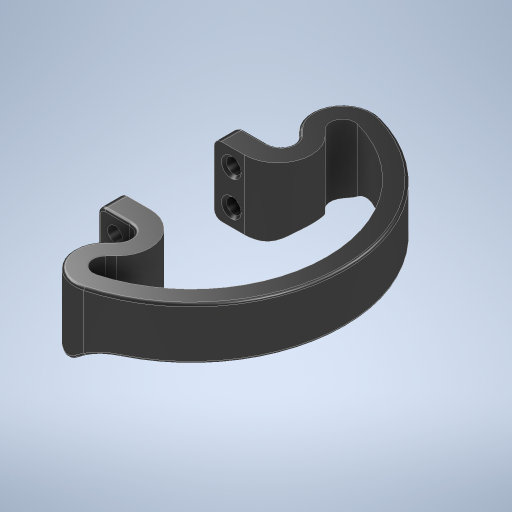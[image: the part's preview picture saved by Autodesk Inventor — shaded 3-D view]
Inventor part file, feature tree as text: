
AUTODESK INVENTOR PART (.ipt)
format: ipt  version: 2024.2 (Build 282272000, 272)  size: 499,200 bytes
history: native  units: mm
features: extrude x3, fillet x3, sketch x3, mirror x1, chamfer x1
ambient origin geometry x8: Origin, YZ Plane, XZ Plane, XY Plane, X Axis, Y Axis, Z Axis, Center Point
bodies: Solid1 (feature_tree)
feature tree (11):
  extrude  "Extrusion1"  Depth=10.0mm
  extrude  "Extrusion2"  Depth=10.0mm
  fillet  "Fillet1"  Radius=1.0mm
  extrude  "Extrusion3"  Depth=3.0mm
  mirror  "Mirror1"
  fillet  "Fillet2"  Radius=1.0mm
  fillet  "Fillet3"  Radius=9.0mm
  chamfer  "Chamfer1"  Distance=38.5mm
  sketch  "Sketch1"  dims[d0=10.0mm d1=125.425516mm]
  sketch  "Sketch2"  dims[d2=10.0mm d3=12.0mm d4=1.0mm]
  sketch  "Sketch3"  dims[d5=5.5mm d6=3.0mm d7=1.0mm d8=9.0mm d9=38.5mm d12=51.3mm d13=14.412758mm d15=7.5mm d16=7.5mm d17=45.0deg d18=28.25mm d19=0.0mm d20=12.0mm d22=1.0mm d23=6.1mm d24=28.5mm d25=0.0mm d26=14.0mm d27=3.0mm d30=36.0mm d31=14.0mm d32=20.0mm d33=19.0mm d34=2.0mm d35=0.0mm d36=0.0mm d37=10.0mm d38=1.0mm d39=28.25mm d40=14.25mm d42=5.0mm d43=1.0mm d44=2.0mm d45=45.0deg d46=1.0mm d47=80.0mm d28=0.0mm d29=0.0mm]
